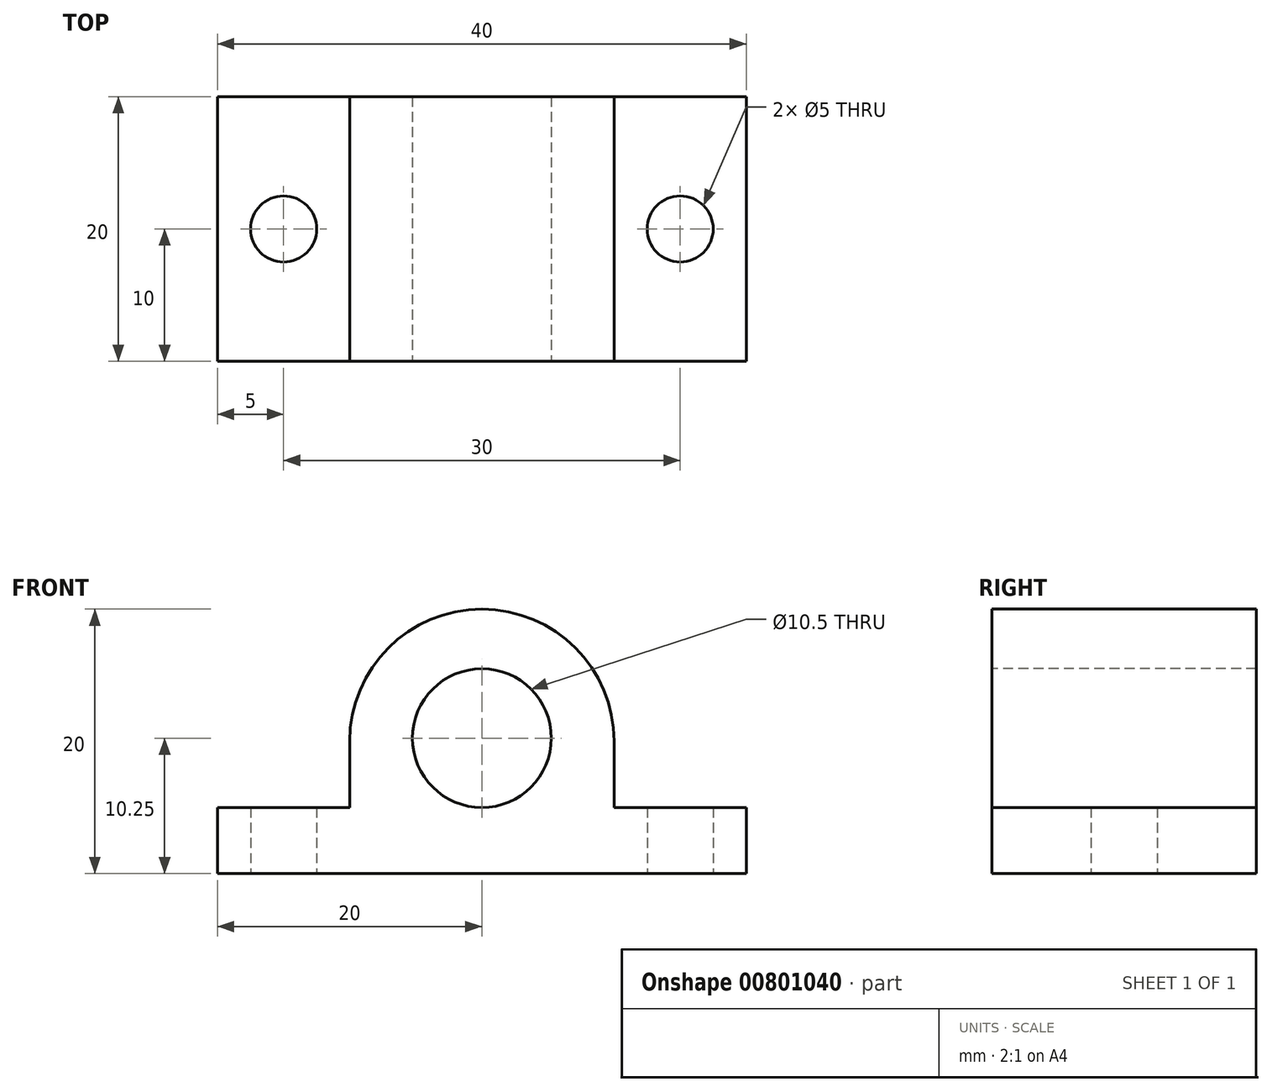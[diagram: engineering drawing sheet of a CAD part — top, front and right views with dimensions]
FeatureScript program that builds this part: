
annotation { "Feature Type Name" : "Feature", "Feature Type Description" : "" }
export const myFeature = defineFeature(function(context is Context, id is Id, definition is map)
    precondition{}
    {
        {
            var Q0;
            Q0=qCreatedBy(makeId("Top.planeOp"),FACE);
            var sketch = newSketch(context, id + "F0", { "sketchPlane" : qUnion([Q0])});
            skLineSegment(sketch, "E0.bottom", {"start": v(20, -10) * mm, "end": v(-20, -10) * mm});
            skLineSegment(sketch, "E0.top", {"start": v(20, 10) * mm, "end": v(-20, 10) * mm});
            skLineSegment(sketch, "E0.left", {"start": v(20, -10) * mm, "end": v(20, 10) * mm});
            skLineSegment(sketch, "E0.right", {"start": v(-20, -10) * mm, "end": v(-20, 10) * mm});
            skPoint(sketch, "E0.middle", {"position": v(0, 0) * mm});
            skCircle(sketch, "E1", {"center": v(15, 0) * mm, "radius": 2.5 * mm});
            skCircle(sketch, "E2", {"center": v(-15, 0) * mm, "radius": 2.5 * mm});
            skSolve(sketch);
        }
        {
            var Q0;
            Q0=makeQuery(id+"F0.imprint","IMPRINT",FACE,{"disambiguationData":[TD([[makeQuery(id+"F0.imprint","IMPRINT",EDGE,{"derivedFrom":sQuery(id+"F0.wireOp",EDGE,"E0.bottom")}),-1.0]])]});
            extrude(context, id + "F1", {"entities" : qUnion([Q0]), "depth" : 5 * mm, "offsetDistance" : 25 * mm});
        }
        {
            var Q0;
            Q0=makeQuery(id+"F1.opExtrude","CAP_FACE",FACE,{"disambiguationData":[OSD([sQuery(id+"F0.wireOp",EDGE,"E0.bottom"),sQuery(id+"F0.wireOp",EDGE,"E0.top"),sQuery(id+"F0.wireOp",EDGE,"E0.left"),sQuery(id+"F0.wireOp",EDGE,"E0.right"),sQuery(id+"F0.wireOp",EDGE,"E1"),sQuery(id+"F0.wireOp",EDGE,"E2")])],"isStart":false});
            var sketch = newSketch(context, id + "F2", { "sketchPlane" : qUnion([Q0])});
            skLineSegment(sketch, "E3.bottom", {"start": v(10, 10) * mm, "end": v(-10, 10) * mm});
            skLineSegment(sketch, "E3.top", {"start": v(10, -10) * mm, "end": v(-10, -10) * mm});
            skLineSegment(sketch, "E3.left", {"start": v(10, 10) * mm, "end": v(10, -10) * mm});
            skLineSegment(sketch, "E3.right", {"start": v(-10, 10) * mm, "end": v(-10, -10) * mm});
            skSolve(sketch);
        }
        {
            var Q0;
            Q0=makeQuery(id+"F2.imprint","IMPRINT",FACE,{"disambiguationData":[TD([[makeQuery(id+"F2.imprint","IMPRINT",EDGE,{"derivedFrom":sQuery(id+"F2.wireOp",EDGE,"E3.bottom")}),1.0]])]});
            extrude(context, id + "F3", {"entities" : qUnion([Q0]), "operationType" : NewBodyOperationType.ADD, "depth" : 15 * mm, "offsetDistance" : 25 * mm});
        }
        {
            var Q0;
            Q0=makeQuery(id+"F3.boolean.opBoolean","MERGE",FACE,{"derivedFrom":[makeQuery(id+"F1.opExtrude","SWEPT_FACE",FACE,{"disambiguationData":[OSD([sQuery(id+"F0.wireOp",EDGE,"E0.bottom")])]}),makeQuery(id+"F3.opExtrude","SWEPT_FACE",FACE,{"disambiguationData":[OSD([sQuery(id+"F2.wireOp",EDGE,"E3.top")])]})]});
            var sketch = newSketch(context, id + "F4", { "sketchPlane" : qUnion([Q0])});
            skCircle(sketch, "E4", {"center": v(0, 10.25) * mm, "radius": 5.25 * mm});
            skSolve(sketch);
        }
        {
            var Q0;
            Q0 = qSketchRegion(id + "F4", true);
            extrude(context, id + "F5", {"entities" : qUnion([Q0]), "operationType" : NewBodyOperationType.REMOVE, "oppositeDirection" : true, "depth" : 25 * mm, "offsetDistance" : 25 * mm});
        }
        {
            var Q0;
            Q0=makeQuery(id+"F3.opExtrude","CAP_EDGE",EDGE,{"disambiguationData":[OSD([sQuery(id+"F2.wireOp",EDGE,"E3.right")])],"isStart":false});
            var Q1;
            Q1=makeQuery(id+"F3.opExtrude","CAP_EDGE",EDGE,{"disambiguationData":[OSD([sQuery(id+"F2.wireOp",EDGE,"E3.left")])],"isStart":false});
            fillet(context, id + "F6", {"entities" : qUnion([Q0, Q1]), "radius" : 10 * mm, "tangentPropagation" : true, "allowEdgeOverflow" : false});
        }
    });
